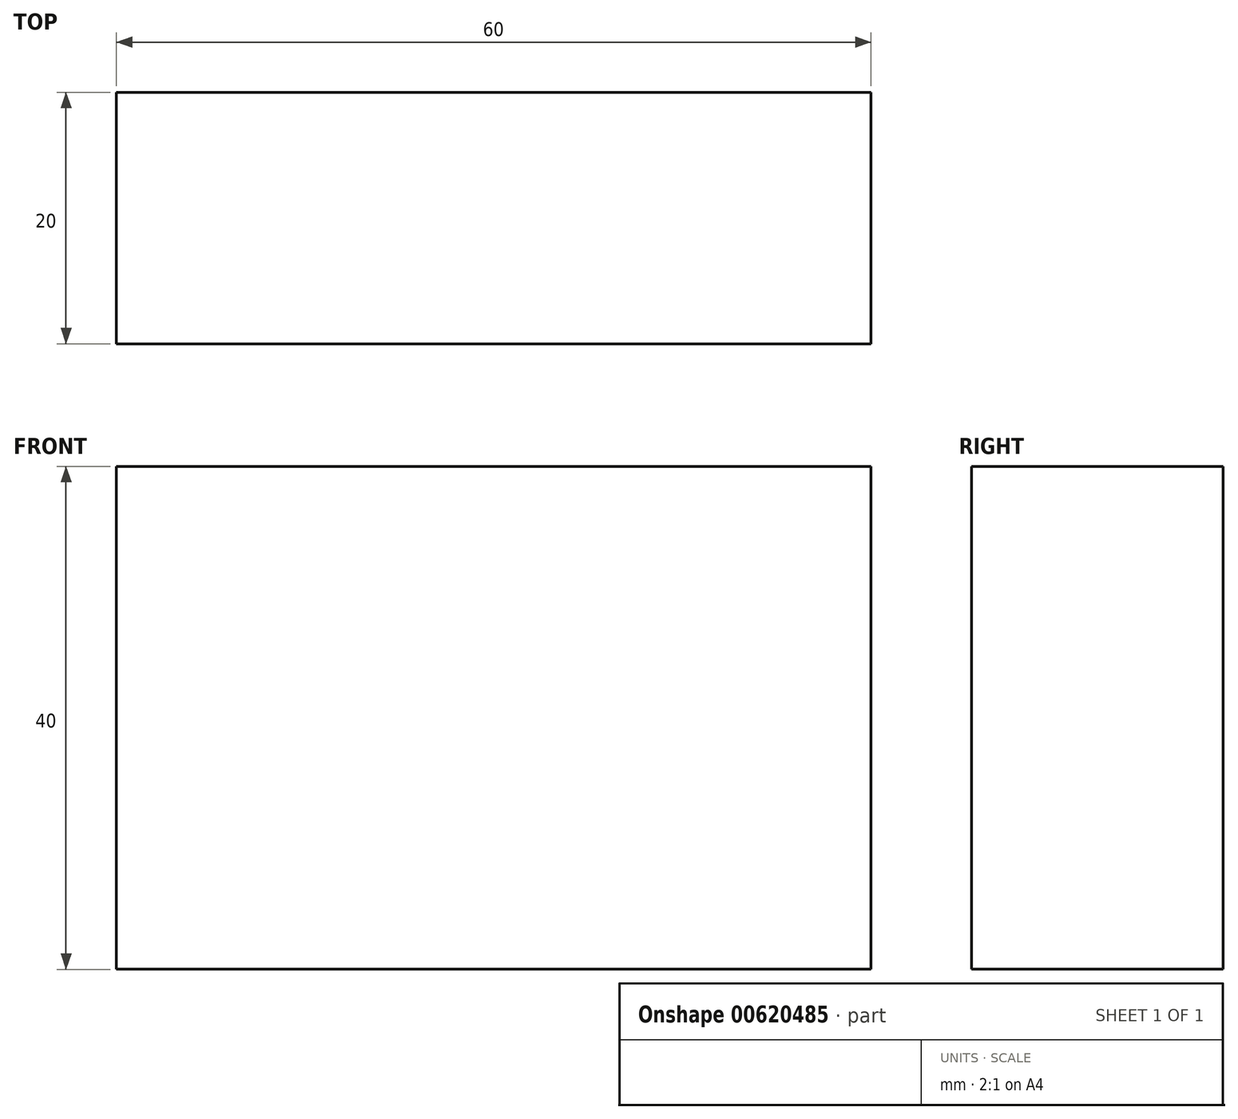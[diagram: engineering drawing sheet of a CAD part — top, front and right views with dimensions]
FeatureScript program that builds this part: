
annotation { "Feature Type Name" : "Feature", "Feature Type Description" : "" }
export const myFeature = defineFeature(function(context is Context, id is Id, definition is map)
    precondition{}
    {
        {
            var Q0;
            Q0=qCreatedBy(makeId("Front.planeOp"),FACE);
            var sketch = newSketch(context, id + "F0", { "sketchPlane" : qUnion([Q0])});
            skLineSegment(sketch, "E0", {"start": v(-39.6, 41.37) * mm, "end": v(20.4, 41.37) * mm});
            skLineSegment(sketch, "E1", {"start": v(20.4, 41.37) * mm, "end": v(20.4, 1.37) * mm});
            skLineSegment(sketch, "E2", {"start": v(20.4, 1.37) * mm, "end": v(-39.6, 1.37) * mm});
            skLineSegment(sketch, "E3", {"start": v(-39.6, 1.37) * mm, "end": v(-39.6, 41.37) * mm});
            skSolve(sketch);
        }
        {
            var Q0;
            Q0 = qSketchRegion(id + "F0", true);
            extrude(context, id + "F1", {"entities" : qUnion([Q0]), "depth" : 20 * mm, "offsetDistance" : 25 * mm});
        }
    });
